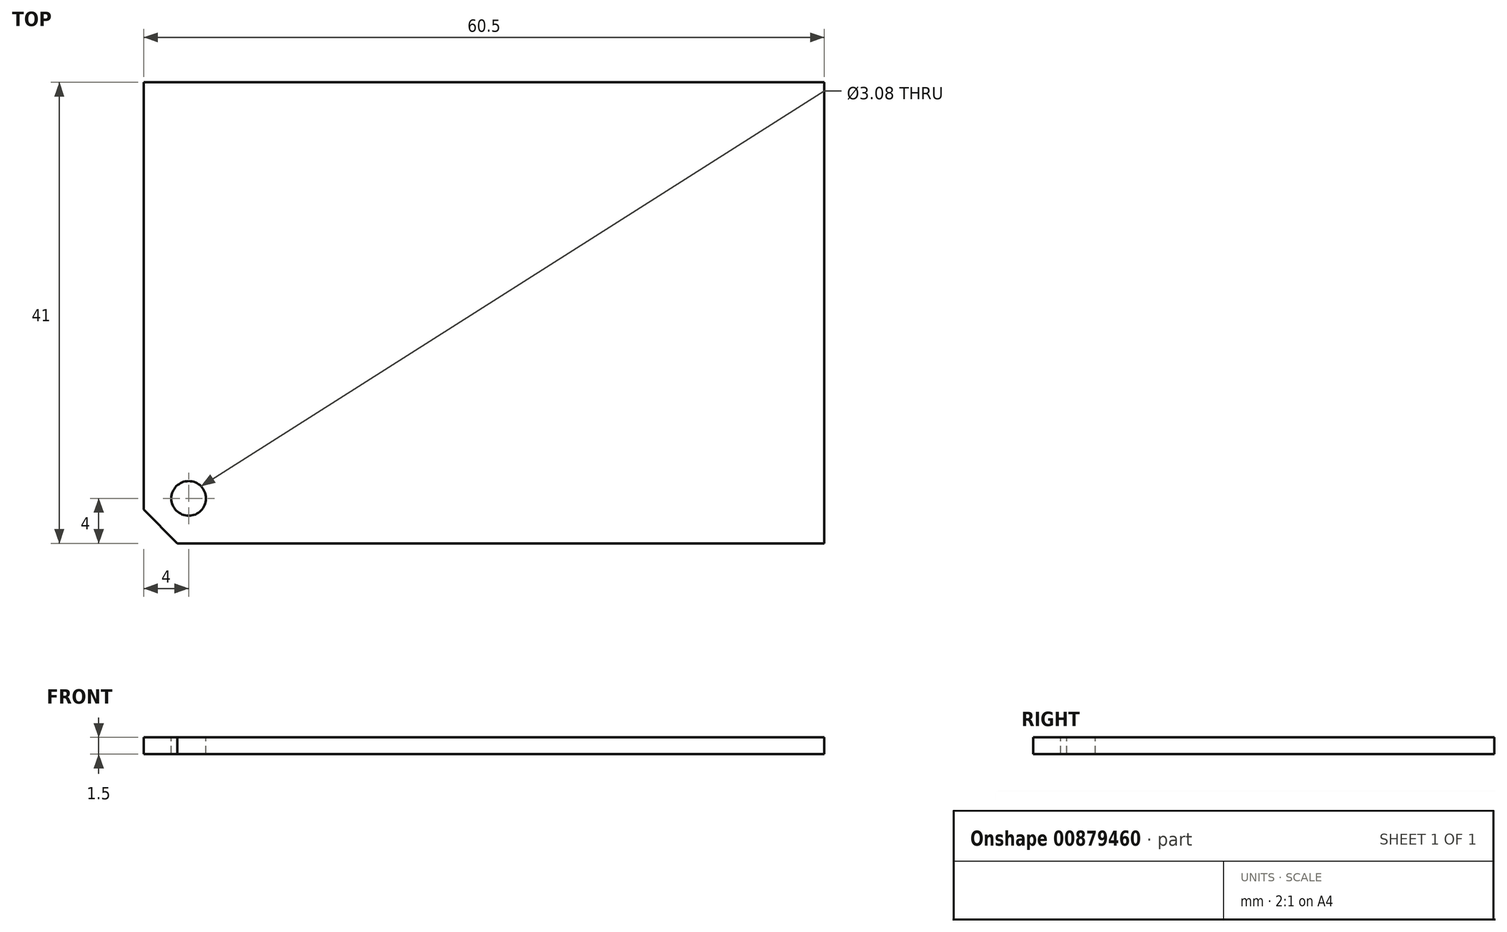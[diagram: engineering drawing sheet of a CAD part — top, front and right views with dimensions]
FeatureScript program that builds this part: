
annotation { "Feature Type Name" : "Feature", "Feature Type Description" : "" }
export const myFeature = defineFeature(function(context is Context, id is Id, definition is map)
    precondition{}
    {
        {
            var Q0;
            Q0=qCreatedBy(makeId("Top.planeOp"),FACE);
            var sketch = newSketch(context, id + "F0", { "sketchPlane" : qUnion([Q0])});
            skLineSegment(sketch, "E0.bottom", {"start": v(0, 0) * mm, "end": v(60.5, 0) * mm});
            skLineSegment(sketch, "E0.top", {"start": v(0, 41) * mm, "end": v(60.5, 41) * mm});
            skLineSegment(sketch, "E0.left", {"start": v(0, 0) * mm, "end": v(0, 41) * mm});
            skLineSegment(sketch, "E0.right", {"start": v(60.5, 0) * mm, "end": v(60.5, 41) * mm});
            skSolve(sketch);
        }
        {
            var Q0;
            Q0 = qSketchRegion(id + "F0", true);
            extrude(context, id + "F1", {"entities" : qUnion([Q0]), "depth" : 1.5 * mm, "offsetDistance" : 25 * mm});
        }
        {
            var Q0;
            Q0=makeQuery(id+"F1.opExtrude","SWEPT_EDGE",EDGE,{"disambiguationData":[OSD([sQuery(id+"F0.wireOp",EDGE,"E0.bottom"),sQuery(id+"F0.wireOp",EDGE,"E0.left")])]});
            chamfer(context, id + "F2", {"entities" : qUnion([Q0]), "width" : 3 * mm, "tangentPropagation" : true});
        }
        {
            var Q0;
            Q0=makeQuery(id+"F1.opExtrude","CAP_FACE",FACE,{"disambiguationData":[OSD([sQuery(id+"F0.wireOp",EDGE,"E0.bottom"),sQuery(id+"F0.wireOp",EDGE,"E0.top"),sQuery(id+"F0.wireOp",EDGE,"E0.left"),sQuery(id+"F0.wireOp",EDGE,"E0.right")])],"isStart":false});
            var sketch = newSketch(context, id + "F3", { "sketchPlane" : qUnion([Q0])});
            skCircle(sketch, "E1", {"center": v(4, 4) * mm, "radius": 1.54 * mm});
            skSolve(sketch);
        }
        {
            var Q0;
            Q0 = qSketchRegion(id + "F3", true);
            extrude(context, id + "F4", {"entities" : qUnion([Q0]), "operationType" : NewBodyOperationType.REMOVE, "endBound" : BoundingType.UP_TO_NEXT, "oppositeDirection" : true, "depth" : 18.6 * mm, "offsetDistance" : 25 * mm});
        }
    });
